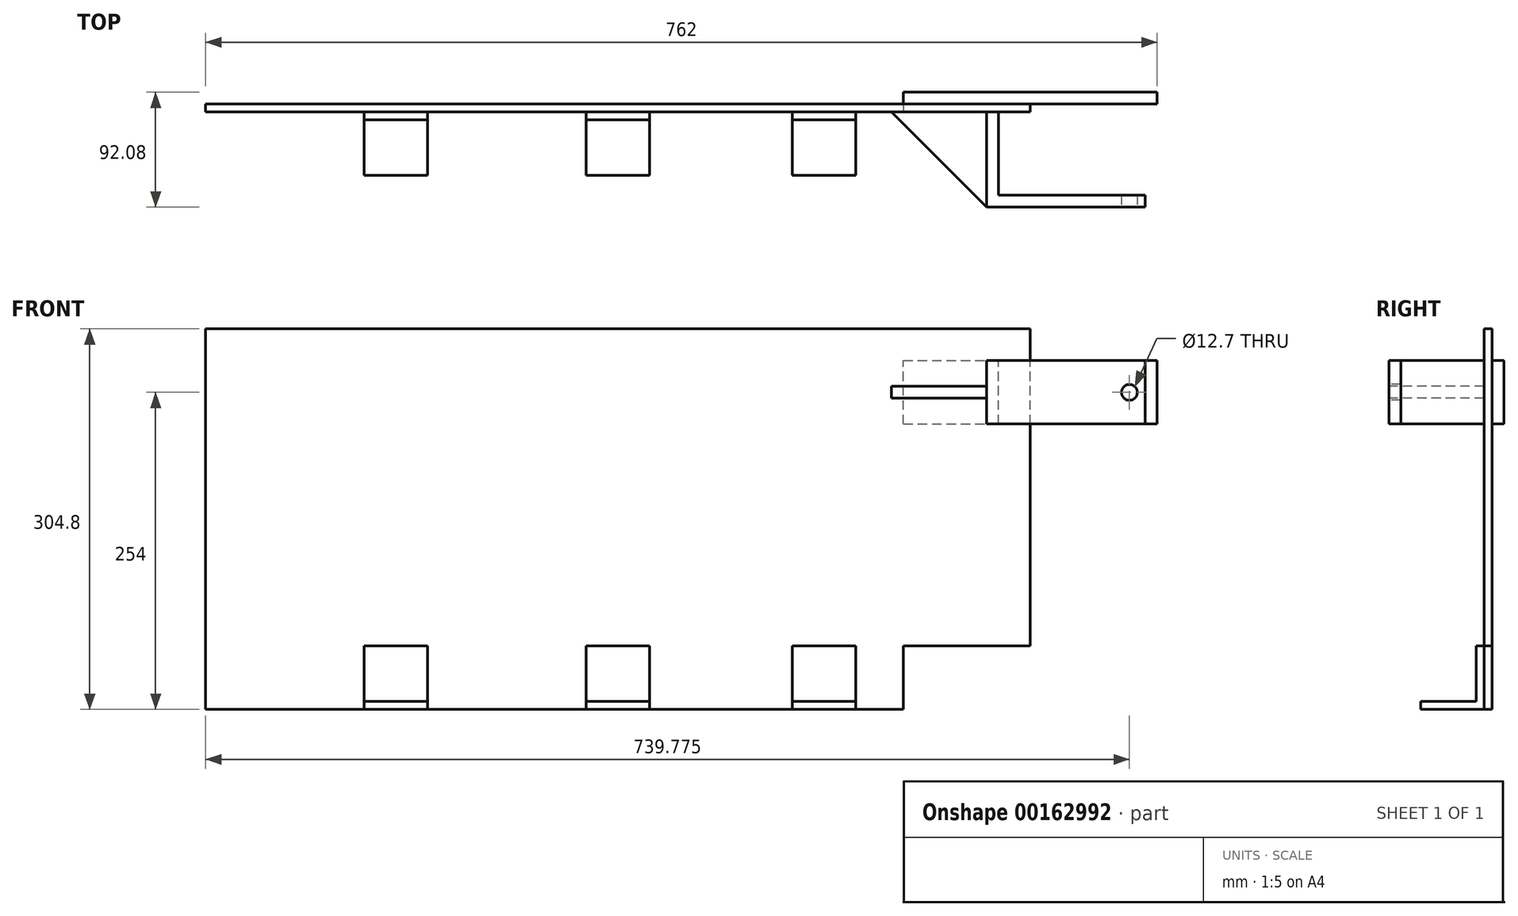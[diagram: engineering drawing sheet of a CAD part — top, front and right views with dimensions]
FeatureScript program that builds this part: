
annotation { "Feature Type Name" : "Feature", "Feature Type Description" : "" }
export const myFeature = defineFeature(function(context is Context, id is Id, definition is map)
    precondition{}
    {
        {
            var Q0;
            Q0=qCreatedBy(makeId("Front.planeOp"),FACE);
            var sketch = newSketch(context, id + "F0", { "sketchPlane" : qUnion([Q0])});
            skLineSegment(sketch, "E0.bottom", {"start": v(330.2, -152.4) * mm, "end": v(-330.2, -152.4) * mm});
            skLineSegment(sketch, "E0.top", {"start": v(330.2, 152.4) * mm, "end": v(-330.2, 152.4) * mm});
            skLineSegment(sketch, "E0.left", {"start": v(330.2, -152.4) * mm, "end": v(330.2, 152.4) * mm});
            skLineSegment(sketch, "E0.right", {"start": v(-330.2, -152.4) * mm, "end": v(-330.2, 152.4) * mm});
            skPoint(sketch, "E0.middle", {"position": v(0, 0) * mm});
            skSolve(sketch);
        }
        {
            var Q0;
            Q0=makeQuery(id+"F0.imprint","IMPRINT",FACE,{"disambiguationData":[TD([[makeQuery(id+"F0.imprint","IMPRINT",EDGE,{"derivedFrom":sQuery(id+"F0.wireOp",EDGE,"E0.bottom")}),-1.0]])]});
            extrude(context, id + "F1", {"entities" : qUnion([Q0]), "depth" : 6.35 * mm});
        }
        {
            var Q0;
            Q0=makeQuery(id+"F1.opExtrude","CAP_FACE",FACE,{"disambiguationData":[OSD([sQuery(id+"F0.wireOp",EDGE,"E0.bottom"),sQuery(id+"F0.wireOp",EDGE,"E0.top"),sQuery(id+"F0.wireOp",EDGE,"E0.left"),sQuery(id+"F0.wireOp",EDGE,"E0.right")])],"isStart":false});
            var sketch = newSketch(context, id + "F2", { "sketchPlane" : qUnion([Q0])});
            skLineSegment(sketch, "E1.bottom", {"start": v(-203.2, -152.4) * mm, "end": v(-152.4, -152.4) * mm});
            skLineSegment(sketch, "E1.top", {"start": v(-203.2, -101.6) * mm, "end": v(-152.4, -101.6) * mm});
            skLineSegment(sketch, "E1.left", {"start": v(-203.2, -152.4) * mm, "end": v(-203.2, -101.6) * mm});
            skLineSegment(sketch, "E1.right", {"start": v(-152.4, -152.4) * mm, "end": v(-152.4, -101.6) * mm});
            skLineSegment(sketch, "E2.bottom", {"start": v(139.7, -152.4) * mm, "end": v(190.5, -152.4) * mm});
            skLineSegment(sketch, "E2.top", {"start": v(139.7, -101.6) * mm, "end": v(190.5, -101.6) * mm});
            skLineSegment(sketch, "E2.left", {"start": v(139.7, -152.4) * mm, "end": v(139.7, -101.6) * mm});
            skLineSegment(sketch, "E2.right", {"start": v(190.5, -152.4) * mm, "end": v(190.5, -101.6) * mm});
            skLineSegment(sketch, "E3.bottom", {"start": v(25.4, -101.6) * mm, "end": v(-25.4, -101.6) * mm});
            skLineSegment(sketch, "E3.left", {"start": v(25.4, -101.6) * mm, "end": v(25.4, -152.4) * mm});
            skLineSegment(sketch, "E3.right", {"start": v(-25.4, -101.6) * mm, "end": v(-25.4, -152.4) * mm});
            skPoint(sketch, "E3.middle", {"position": v(0, -139.2) * mm});
            skPoint(sketch, "E3.middle.positionSnap0", {"position": v(0, -152.4) * mm});
            skPoint(sketch, "E3.centerSnap0", {"position": v(0, -152.4) * mm});
            skLineSegment(sketch, "E4", {"start": v(-25.4, -152.4) * mm, "end": v(25.4, -152.4) * mm});
            skPoint(sketch, "E3.top.end.orphan", {"position": v(-25.4, -176.82) * mm});
            skPoint(sketch, "E5.orphan", {"position": v(25.4, -176.82) * mm});
            skSolve(sketch);
        }
        {
            var Q0;
            Q0=makeQuery(id+"F2.imprint","IMPRINT",FACE,{"disambiguationData":[TD([[makeQuery(id+"F2.imprint","IMPRINT",EDGE,{"derivedFrom":sQuery(id+"F2.wireOp",EDGE,"E2.bottom")}),-1.0]])]});
            var Q1;
            Q1=makeQuery(id+"F2.imprint","IMPRINT",FACE,{"disambiguationData":[TD([[makeQuery(id+"F2.imprint","IMPRINT",EDGE,{"derivedFrom":sQuery(id+"F2.wireOp",EDGE,"E3.bottom")}),1.0]])]});
            var Q2;
            Q2=makeQuery(id+"F2.imprint","IMPRINT",FACE,{"disambiguationData":[TD([[makeQuery(id+"F2.imprint","IMPRINT",EDGE,{"derivedFrom":sQuery(id+"F2.wireOp",EDGE,"E1.bottom")}),-1.0]])]});
            extrude(context, id + "F3", {"entities" : qUnion([Q0, Q1, Q2]), "operationType" : NewBodyOperationType.ADD, "depth" : 6.35 * mm});
        }
        {
            var Q0;
            Q0=makeQuery(id+"F3.opExtrude","CAP_FACE",FACE,{"disambiguationData":[OSD([sQuery(id+"F2.wireOp",EDGE,"E1.bottom"),sQuery(id+"F2.wireOp",EDGE,"E1.top"),sQuery(id+"F2.wireOp",EDGE,"E1.left"),sQuery(id+"F2.wireOp",EDGE,"E1.right")])],"isStart":false});
            var sketch = newSketch(context, id + "F4", { "sketchPlane" : qUnion([Q0])});
            skLineSegment(sketch, "E6.bottom", {"start": v(-203.2, -146.05) * mm, "end": v(-152.4, -146.05) * mm});
            skLineSegment(sketch, "E6.top", {"start": v(-203.2, -152.4) * mm, "end": v(-152.4, -152.4) * mm});
            skLineSegment(sketch, "E6.left", {"start": v(-203.2, -146.05) * mm, "end": v(-203.2, -152.4) * mm});
            skLineSegment(sketch, "E6.right", {"start": v(-152.4, -146.05) * mm, "end": v(-152.4, -152.4) * mm});
            skSolve(sketch);
        }
        {
            var Q0;
            Q0=makeQuery(id+"F3.opExtrude","CAP_FACE",FACE,{"disambiguationData":[OSD([sQuery(id+"F2.wireOp",EDGE,"E3.bottom"),sQuery(id+"F2.wireOp",EDGE,"E3.left"),sQuery(id+"F2.wireOp",EDGE,"E3.right"),sQuery(id+"F2.wireOp",EDGE,"E4")])],"isStart":false});
            var sketch = newSketch(context, id + "F5", { "sketchPlane" : qUnion([Q0])});
            skLineSegment(sketch, "E7.bottom", {"start": v(-25.4, -146.05) * mm, "end": v(25.4, -146.05) * mm});
            skLineSegment(sketch, "E7.top", {"start": v(-25.4, -152.4) * mm, "end": v(25.4, -152.4) * mm});
            skLineSegment(sketch, "E7.left", {"start": v(-25.4, -146.05) * mm, "end": v(-25.4, -152.4) * mm});
            skLineSegment(sketch, "E7.right", {"start": v(25.4, -146.05) * mm, "end": v(25.4, -152.4) * mm});
            skSolve(sketch);
        }
        {
            var Q0;
            Q0=makeQuery(id+"F3.opExtrude","CAP_FACE",FACE,{"disambiguationData":[OSD([sQuery(id+"F2.wireOp",EDGE,"E2.bottom"),sQuery(id+"F2.wireOp",EDGE,"E2.top"),sQuery(id+"F2.wireOp",EDGE,"E2.left"),sQuery(id+"F2.wireOp",EDGE,"E2.right")])],"isStart":false});
            var sketch = newSketch(context, id + "F6", { "sketchPlane" : qUnion([Q0])});
            skLineSegment(sketch, "E8.bottom", {"start": v(139.7, -146.05) * mm, "end": v(190.5, -146.05) * mm});
            skLineSegment(sketch, "E8.top", {"start": v(139.7, -152.4) * mm, "end": v(190.5, -152.4) * mm});
            skLineSegment(sketch, "E8.left", {"start": v(139.7, -146.05) * mm, "end": v(139.7, -152.4) * mm});
            skLineSegment(sketch, "E8.right", {"start": v(190.5, -146.05) * mm, "end": v(190.5, -152.4) * mm});
            skSolve(sketch);
        }
        {
            var Q0;
            Q0=makeQuery(id+"F4.imprint","IMPRINT",FACE,{"disambiguationData":[TD([[makeQuery(id+"F4.imprint","IMPRINT",EDGE,{"derivedFrom":sQuery(id+"F4.wireOp",EDGE,"E6.bottom")}),-1.0]])]});
            var Q1;
            Q1=makeQuery(id+"F5.imprint","IMPRINT",FACE,{"disambiguationData":[TD([[makeQuery(id+"F5.imprint","IMPRINT",EDGE,{"derivedFrom":sQuery(id+"F5.wireOp",EDGE,"E7.bottom")}),-1.0]])]});
            var Q2;
            Q2=makeQuery(id+"F6.imprint","IMPRINT",FACE,{"disambiguationData":[TD([[makeQuery(id+"F6.imprint","IMPRINT",EDGE,{"derivedFrom":sQuery(id+"F6.wireOp",EDGE,"E8.bottom")}),-1.0]])]});
            extrude(context, id + "F7", {"entities" : qUnion([Q0, Q1, Q2]), "operationType" : NewBodyOperationType.ADD, "depth" : 44.45 * mm});
        }
        {
            var Q0;
            Q0=makeQuery(id+"F1.opExtrude","CAP_FACE",FACE,{"disambiguationData":[OSD([sQuery(id+"F0.wireOp",EDGE,"E0.bottom"),sQuery(id+"F0.wireOp",EDGE,"E0.top"),sQuery(id+"F0.wireOp",EDGE,"E0.left"),sQuery(id+"F0.wireOp",EDGE,"E0.right")])],"isStart":true});
            var sketch = newSketch(context, id + "F8", { "sketchPlane" : qUnion([Q0])});
            skLineSegment(sketch, "E9.bottom", {"start": v(-228.6, 76.2) * mm, "end": v(-431.8, 76.2) * mm});
            skLineSegment(sketch, "E9.top", {"start": v(-228.6, 127) * mm, "end": v(-431.8, 127) * mm});
            skLineSegment(sketch, "E9.left", {"start": v(-228.6, 76.2) * mm, "end": v(-228.6, 127) * mm});
            skLineSegment(sketch, "E9.right", {"start": v(-431.8, 76.2) * mm, "end": v(-431.8, 127) * mm});
            skPoint(sketch, "E9.middle", {"position": v(-330.2, 101.6) * mm});
            skSolve(sketch);
        }
        {
            var Q0;
            {var subQ0=sQuery(id+"F8.wireOp",EDGE,"E9.right");Q0=makeQuery(id+"F8.imprint","IMPRINT",FACE,{"disambiguationData":[TD([[makeQuery(id+"F8.imprint","IMPRINT",EDGE,{"derivedFrom":subQ0}),-1.0]])]});}
            var Q1;
            {var subQ0=sQuery(id+"F8.wireOp",EDGE,"E9.left");Q1=makeQuery(id+"F8.imprint","IMPRINT",FACE,{"disambiguationData":[TD([[makeQuery(id+"F8.imprint","IMPRINT",EDGE,{"derivedFrom":subQ0}),1.0]])]});}
            extrude(context, id + "F9", {"entities" : qUnion([Q0, Q1]), "operationType" : NewBodyOperationType.ADD, "depth" : 9.52 * mm});
        }
        {
            var Q0;
            Q0=makeQuery(id+"F1.opExtrude","CAP_FACE",FACE,{"disambiguationData":[OSD([sQuery(id+"F0.wireOp",EDGE,"E0.bottom"),sQuery(id+"F0.wireOp",EDGE,"E0.top"),sQuery(id+"F0.wireOp",EDGE,"E0.left"),sQuery(id+"F0.wireOp",EDGE,"E0.right")])],"isStart":false});
            var sketch = newSketch(context, id + "F10", { "sketchPlane" : qUnion([Q0])});
            skLineSegment(sketch, "E10.bottom", {"start": v(330.2, -152.4) * mm, "end": v(228.6, -152.4) * mm});
            skLineSegment(sketch, "E10.top", {"start": v(330.2, -101.6) * mm, "end": v(228.6, -101.6) * mm});
            skLineSegment(sketch, "E10.left", {"start": v(330.2, -152.4) * mm, "end": v(330.2, -101.6) * mm});
            skLineSegment(sketch, "E10.right", {"start": v(228.6, -152.4) * mm, "end": v(228.6, -101.6) * mm});
            skSolve(sketch);
        }
        {
            var Q0;
            Q0 = qSketchRegion(id + "F10", true);
            extrude(context, id + "F11", {"entities" : qUnion([Q0]), "operationType" : NewBodyOperationType.REMOVE, "oppositeDirection" : true, "depth" : 25.4 * mm});
        }
        {
            var Q0;
            Q0=makeQuery(id+"F1.opExtrude","CAP_FACE",FACE,{"disambiguationData":[OSD([sQuery(id+"F0.wireOp",EDGE,"E0.bottom"),sQuery(id+"F0.wireOp",EDGE,"E0.top"),sQuery(id+"F0.wireOp",EDGE,"E0.left"),sQuery(id+"F0.wireOp",EDGE,"E0.right")])],"isStart":false});
            var sketch = newSketch(context, id + "F12", { "sketchPlane" : qUnion([Q0])});
            skLineSegment(sketch, "E11.bottom", {"start": v(295.28, 76.2) * mm, "end": v(304.8, 76.2) * mm});
            skLineSegment(sketch, "E11.top", {"start": v(295.28, 127) * mm, "end": v(304.8, 127) * mm});
            skLineSegment(sketch, "E11.left", {"start": v(295.28, 76.2) * mm, "end": v(295.28, 127) * mm});
            skLineSegment(sketch, "E11.right", {"start": v(304.8, 76.2) * mm, "end": v(304.8, 127) * mm});
            skSolve(sketch);
        }
        {
            var Q0;
            Q0 = qSketchRegion(id + "F12", true);
            extrude(context, id + "F13", {"entities" : qUnion([Q0]), "operationType" : NewBodyOperationType.ADD, "depth" : 76.2 * mm});
        }
        {
            var Q0;
            Q0=makeQuery(id+"F13.opExtrude","SWEPT_FACE",FACE,{"disambiguationData":[OSD([sQuery(id+"F12.wireOp",EDGE,"E11.right")])]});
            var sketch = newSketch(context, id + "F14", { "sketchPlane" : qUnion([Q0])});
            skLineSegment(sketch, "E12.bottom", {"start": v(-82.55, 76.2) * mm, "end": v(-73.02, 76.2) * mm});
            skLineSegment(sketch, "E12.top", {"start": v(-82.55, 127) * mm, "end": v(-73.02, 127) * mm});
            skLineSegment(sketch, "E12.left", {"start": v(-82.55, 76.2) * mm, "end": v(-82.55, 127) * mm});
            skLineSegment(sketch, "E12.right", {"start": v(-73.02, 76.2) * mm, "end": v(-73.02, 127) * mm});
            skSolve(sketch);
        }
        {
            var Q0;
            Q0 = qSketchRegion(id + "F14", true);
            extrude(context, id + "F15", {"entities" : qUnion([Q0]), "operationType" : NewBodyOperationType.ADD, "depth" : 117.47 * mm});
        }
        {
            var Q0;
            Q0=makeQuery(id+"F15.boolean.opBoolean","MERGE",FACE,{"derivedFrom":[makeQuery(id+"F13.opExtrude","CAP_FACE",FACE,{"disambiguationData":[OSD([sQuery(id+"F12.wireOp",EDGE,"E11.bottom"),sQuery(id+"F12.wireOp",EDGE,"E11.top"),sQuery(id+"F12.wireOp",EDGE,"E11.left"),sQuery(id+"F12.wireOp",EDGE,"E11.right")])],"isStart":false}),makeQuery(id+"F15.opExtrude","SWEPT_FACE",FACE,{"disambiguationData":[OSD([sQuery(id+"F14.wireOp",EDGE,"E12.left")])]})]});
            var sketch = newSketch(context, id + "F16", { "sketchPlane" : qUnion([Q0])});
            skCircle(sketch, "E13", {"center": v(409.58, 101.6) * mm, "radius": 6.35 * mm});
            skPoint(sketch, "E13.centerSnap0", {"position": v(422.28, 101.6) * mm});
            skSolve(sketch);
        }
        {
            var Q0;
            Q0 = qSketchRegion(id + "F16", true);
            extrude(context, id + "F17", {"entities" : qUnion([Q0]), "operationType" : NewBodyOperationType.REMOVE, "oppositeDirection" : true, "depth" : 25.4 * mm});
        }
        {
            var Q0;
            Q0=makeQuery(id+"F13.opExtrude","SWEPT_FACE",FACE,{"disambiguationData":[OSD([sQuery(id+"F12.wireOp",EDGE,"E11.left")])]});
            var sketch = newSketch(context, id + "F18", { "sketchPlane" : qUnion([Q0])});
            skLineSegment(sketch, "E14.bottom", {"start": v(6.35, 96.84) * mm, "end": v(82.55, 96.84) * mm});
            skLineSegment(sketch, "E14.top", {"start": v(6.35, 106.36) * mm, "end": v(82.55, 106.36) * mm});
            skLineSegment(sketch, "E14.left", {"start": v(6.35, 96.84) * mm, "end": v(6.35, 106.36) * mm});
            skLineSegment(sketch, "E14.right", {"start": v(158.75, 96.84) * mm, "end": v(158.75, 106.36) * mm});
            skPoint(sketch, "E14.middle", {"position": v(82.55, 101.6) * mm});
            skLineSegment(sketch, "E15", {"start": v(82.55, 106.36) * mm, "end": v(82.55, 96.84) * mm});
            skSolve(sketch);
        }
        {
            var Q0;
            Q0 = qSketchRegion(id + "F18", true);
            extrude(context, id + "F19", {"entities" : qUnion([Q0]), "operationType" : NewBodyOperationType.ADD, "depth" : 76.2 * mm});
        }
        {
            var Q0;
            Q0=makeQuery(id+"F19.opExtrude","SWEPT_FACE",FACE,{"disambiguationData":[OSD([sQuery(id+"F18.wireOp",EDGE,"E14.bottom")])]});
            var sketch = newSketch(context, id + "F20", { "sketchPlane" : qUnion([Q0])});
            skLineSegment(sketch, "E16", {"start": v(219.08, 6.35) * mm, "end": v(295.28, 82.55) * mm});
            skLineSegment(sketch, "E17", {"start": v(295.28, 82.55) * mm, "end": v(295.28, 6.35) * mm});
            skLineSegment(sketch, "E18", {"start": v(295.28, 6.35) * mm, "end": v(219.08, 6.35) * mm});
            skLineSegment(sketch, "E19", {"start": v(219.08, 6.35) * mm, "end": v(219.08, 82.55) * mm});
            skLineSegment(sketch, "E20", {"start": v(219.08, 82.55) * mm, "end": v(295.28, 82.55) * mm});
            skSolve(sketch);
        }
        {
            var Q0;
            Q0=makeQuery(id+"F20.imprint","IMPRINT",FACE,{"disambiguationData":[TD([[makeQuery(id+"F20.imprint","IMPRINT",EDGE,{"derivedFrom":sQuery(id+"F20.wireOp",EDGE,"E16")}),1.0]])]});
            extrude(context, id + "F21", {"entities" : qUnion([Q0]), "operationType" : NewBodyOperationType.REMOVE, "oppositeDirection" : true, "depth" : 25.4 * mm});
        }
    });
